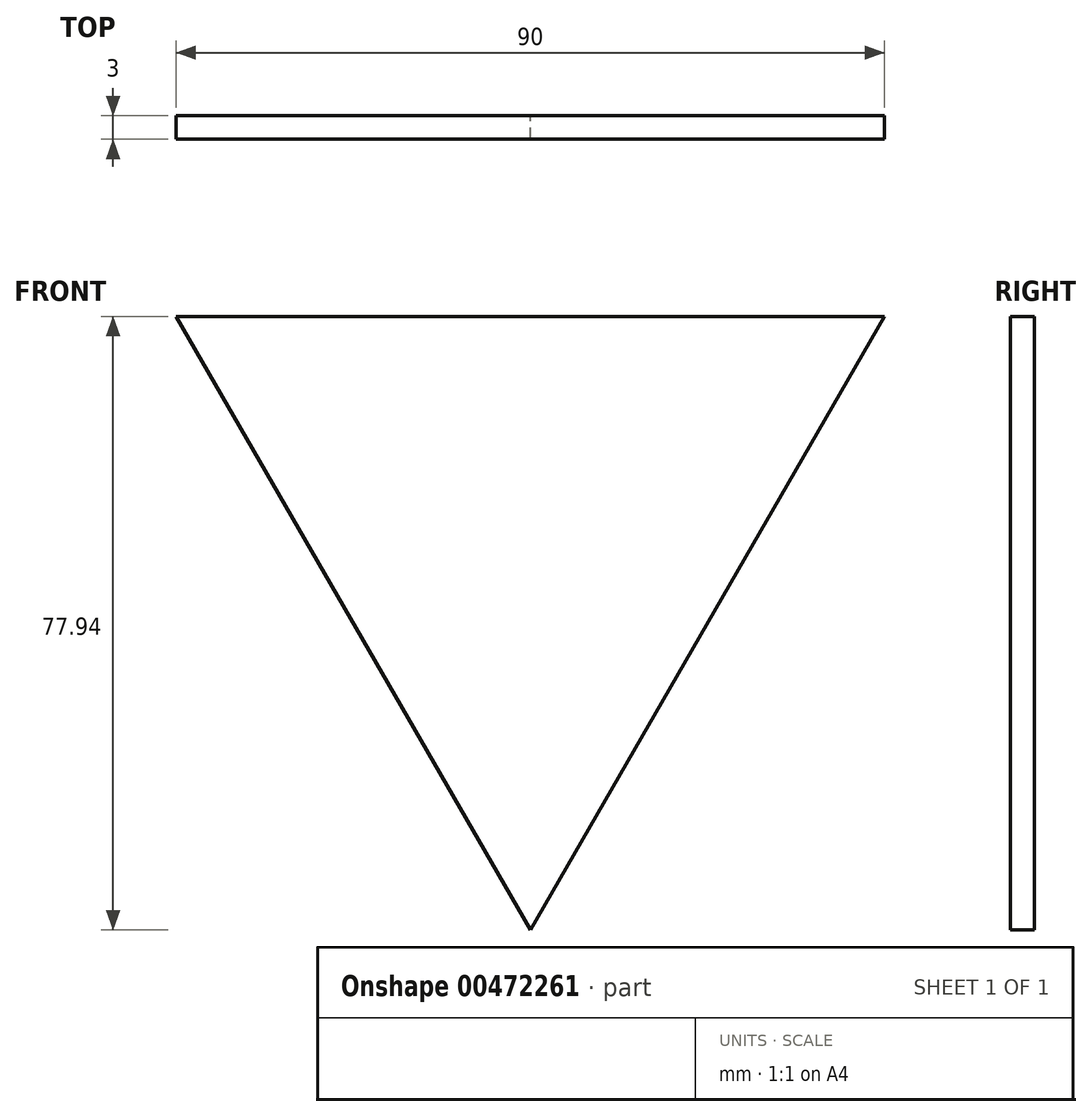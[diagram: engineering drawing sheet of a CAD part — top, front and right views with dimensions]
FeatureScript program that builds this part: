
annotation { "Feature Type Name" : "Feature", "Feature Type Description" : "" }
export const myFeature = defineFeature(function(context is Context, id is Id, definition is map)
    precondition{}
    {
        {
            var Q0;
            Q0=qCreatedBy(makeId("Front.planeOp"),FACE);
            var sketch = newSketch(context, id + "F0", { "sketchPlane" : qUnion([Q0])});
            skCircle(sketch, "E0.cCircle", {"center": v(0, 0) * mm, "radius": 25.98 * mm, "construction": true});
            skLineSegment(sketch, "E0.0", {"start": v(-45, 25.98) * mm, "end": v(45, 25.98) * mm});
            skLineSegment(sketch, "E0.1", {"start": v(45, 25.98) * mm, "end": v(0, -51.96) * mm});
            skLineSegment(sketch, "E0.2", {"start": v(0, -51.96) * mm, "end": v(-45, 25.98) * mm});
            skPoint(sketch, "E0.0.midPoint", {"position": v(0, 25.98) * mm});
            skSolve(sketch);
        }
        {
            var Q0;
            Q0 = qSketchRegion(id + "F0", true);
            extrude(context, id + "F1", {"entities" : qUnion([Q0]), "depth" : 3 * mm});
        }
    });
